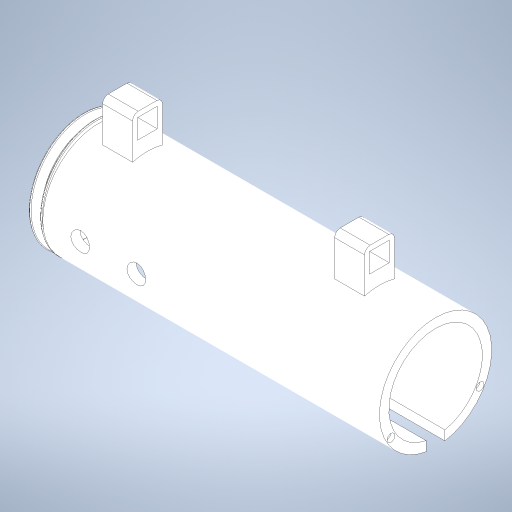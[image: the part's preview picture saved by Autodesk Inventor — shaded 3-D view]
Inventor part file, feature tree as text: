
AUTODESK INVENTOR PART (.ipt)
format: ipt  version: 2023 (Build 270158000, 158)  size: 495,104 bytes
history: native  units: in
note: dims shown in document units (in); Inventor stores cm internally (conversion verified against a paired STEP export)
features: sketch x7, extrude x6, pattern_linear x2, revolve x2, plane x1, fillet x1, mirror x1, thread x1, helix x1, projected_geometry x1
ambient origin geometry x8: Origin, YZ Plane, XZ Plane, XY Plane, X Axis, Y Axis, Z Axis, Center Point
bodies: Solid1 (feature_tree), Solid6 (feature_tree)
feature tree (23):
  sketch  "Sketch1"  dims[d0=1.1811in d1=0.9843in]
  extrude  "Extrusion1"  Depth=0.9843in
  extrude  "Extrusion2"  Depth=3.7402in TaperAngle=0.0deg
  plane  "Work Plane1"
  extrude  "Extrusion4"  Depth=0.0984in
  extrude  "Extrusion5"  Depth=0.3937in
  pattern_linear  "Rectangular Pattern2"  Count1=11 Spacing1=0.0in
  fillet  "Fillet2"  Radius=0.315in
  extrude  "Extrusion6"  Depth=0.3937in
  pattern_linear  "Rectangular Pattern3"  Spacing1=0.1969in  [1 undecoded]
  extrude  "Extrusion7"  Depth=0.3937in TaperAngle=0.0deg
  mirror  "Mirror1"
  thread  "Thread7"  [1 undecoded]
  revolve  "Revolution9"  [1 undecoded]
  revolve  "Revolution10"  [1 undecoded]
  helix  "Coil5"  [1 undecoded]
  sketch  "Sketch6"  dims[d2=0.4921in d3=3.7402in d4=0.0in]
  sketch  "Sketch7"  dims[d5=0.0984in d6=0.0in d19=0.0984in]
  sketch  "Sketch14"  dims[d20=0.0984in d21=0.3937in]
  projected_geometry  "Projected Loop1"
  sketch  "Sketch21"  dims[d22=1.1811in d23=0.9843in d24=0.4921in d25=0.0984in d26=0.0984in d27=4.3307in d28=0.0in]
  sketch  "Sketch22"  dims[d29=0.315in d30=0.315in d31=0.2067in d32=0.2067in d33=0.315in d34=0.0in]
  sketch  "Sketch23"  dims[d35=0.0591in d36=0.7874in d38=2.4409in d39=0.1969in d40=1.9685in d41=0.0in d42=0.5906in d43=0.7874in d45=0.5906in d59=0.3779in d81=0.3779in d94=120.0deg d95=0.0827in d96=0.0079in d97=0.0433in d98=0.0in d99=1.378in d109=0.3779in d130=0.3779in d142=0.1969in d143=0.0in d144=0.3779in d145=0.0189in d146=0.0189in d149=0.1181in d151=0.3779in d153=0.0in d154=0.0in d155=0.1182in d156=0.4331in d157=0.3937in d158=0.0in d159=0.0in d160=0.0in d161=0.0in d162=0.0in d100=0.0344in d101=0.0197in d102=0.0344in d103=0.0344in]
note: 5 required parameter values undecoded (feature->parameter linkage not recoverable at this tier; creation-order binding heuristic only, values carry confidence <= 0.55)